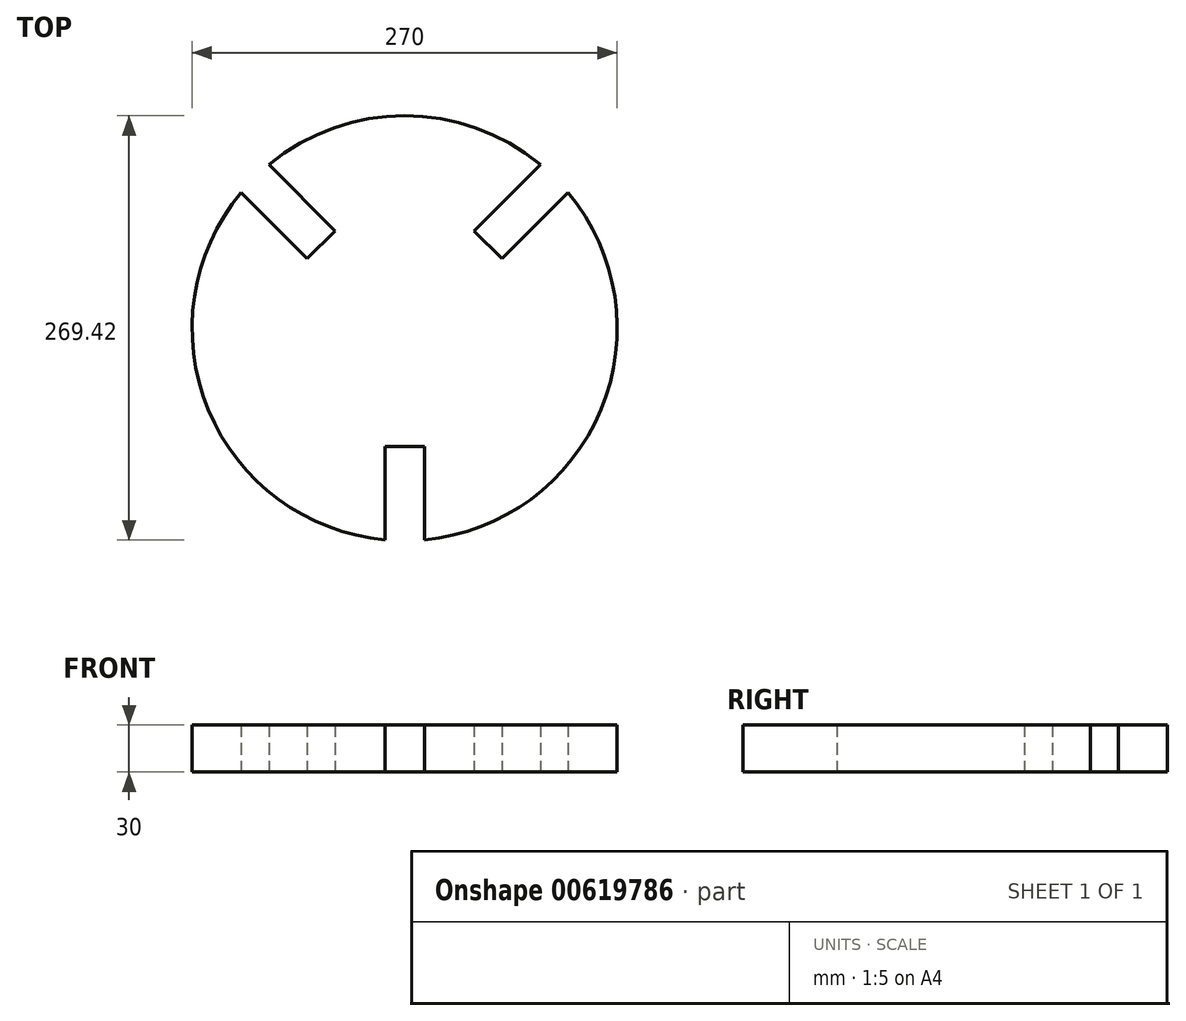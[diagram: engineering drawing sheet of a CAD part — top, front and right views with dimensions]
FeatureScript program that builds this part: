
annotation { "Feature Type Name" : "Feature", "Feature Type Description" : "" }
export const myFeature = defineFeature(function(context is Context, id is Id, definition is map)
    precondition{}
    {
        {
            var Q0;
            Q0=qCreatedBy(makeId("Top.planeOp"),FACE);
            var sketch = newSketch(context, id + "F0", { "sketchPlane" : qUnion([Q0])});
            skPoint(sketch, "E0.middle", {"position": v(0, 0) * mm});
            skLineSegment(sketch, "E1", {"start": v(61.87, 44.2) * mm, "end": v(104.3, 86.62) * mm});
            skLineSegment(sketch, "E2", {"start": v(44.2, 61.87) * mm, "end": v(86.62, 104.3) * mm});
            skLineSegment(sketch, "E3", {"start": v(12.5, -75) * mm, "end": v(12.5, -135) * mm});
            skLineSegment(sketch, "E4", {"start": v(-12.5, -75) * mm, "end": v(-12.5, -135) * mm});
            skLineSegment(sketch, "E5", {"start": v(-12.5, -75) * mm, "end": v(12.5, -75) * mm});
            skLineSegment(sketch, "E6", {"start": v(44.2, 61.87) * mm, "end": v(61.87, 44.2) * mm});
            skLineSegment(sketch, "E7", {"start": v(-44.2, 61.87) * mm, "end": v(-86.62, 104.3) * mm});
            skLineSegment(sketch, "E8", {"start": v(-61.87, 44.2) * mm, "end": v(-104.3, 86.62) * mm});
            skLineSegment(sketch, "E9", {"start": v(-61.87, 44.2) * mm, "end": v(-44.2, 61.87) * mm});
            skArc(sketch, "E10", {"start": v(-103.89, 86.21) * mm, "mid": v(-124.72, -51.66) * mm, "end": v(-12.5, -134.42) * mm});
            skArc(sketch, "E11.trimOffspring", {"start": v(86.21, 103.89) * mm, "mid": v(0, 135) * mm, "end": v(-86.21, 103.89) * mm});
            skArc(sketch, "E12.trimOffspring", {"start": v(12.5, -134.42) * mm, "mid": v(124.72, -51.66) * mm, "end": v(103.89, 86.21) * mm});
            skSolve(sketch);
        }
        {
            var Q0;
            Q0 = qSketchRegion(id + "F0", true);
            extrude(context, id + "F1", {"entities" : qUnion([Q0]), "depth" : 30 * mm, "offsetDistance" : 25 * mm});
        }
    });
